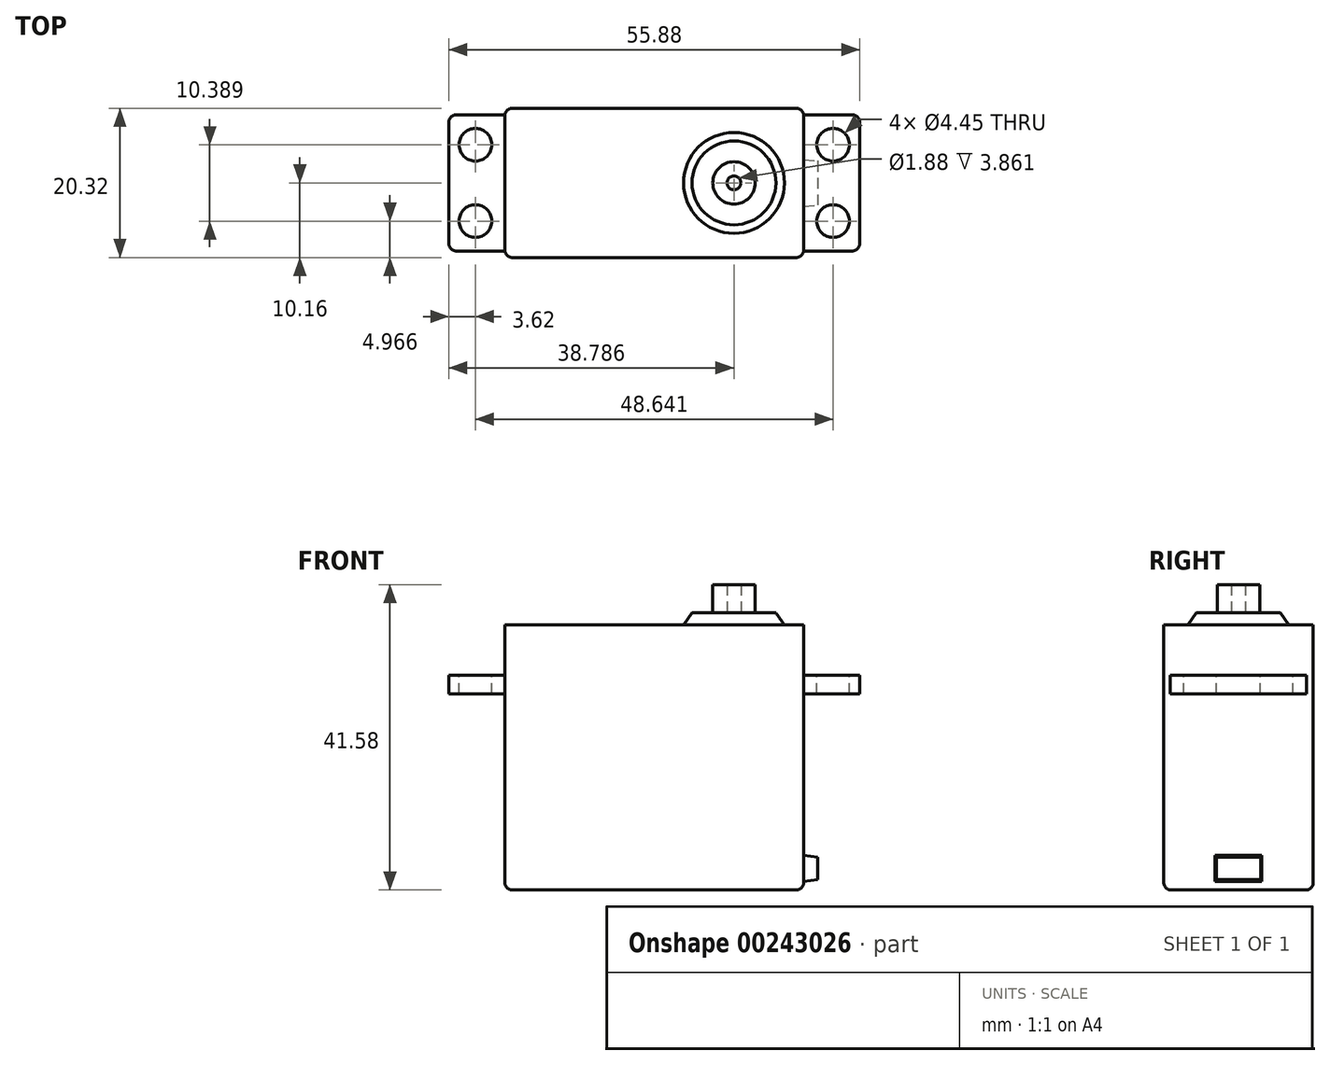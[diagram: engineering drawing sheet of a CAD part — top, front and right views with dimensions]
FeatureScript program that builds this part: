
annotation { "Feature Type Name" : "Feature", "Feature Type Description" : "" }
export const myFeature = defineFeature(function(context is Context, id is Id, definition is map)
    precondition{}
    {
        {
            var Q0;
            Q0=qCreatedBy(makeId("Top.planeOp"),FACE);
            var sketch = newSketch(context, id + "F0", { "sketchPlane" : qUnion([Q0])});
            skLineSegment(sketch, "E0.bottom", {"start": v(20.32, 10.16) * mm, "end": v(-20.32, 10.16) * mm});
            skLineSegment(sketch, "E0.top", {"start": v(20.32, -10.16) * mm, "end": v(-20.32, -10.16) * mm});
            skLineSegment(sketch, "E0.left", {"start": v(20.32, 10.16) * mm, "end": v(20.32, -10.16) * mm});
            skLineSegment(sketch, "E0.right", {"start": v(-20.32, 10.16) * mm, "end": v(-20.32, -10.16) * mm});
            skPoint(sketch, "E0.middle", {"position": v(0, 0) * mm});
            skSolve(sketch);
        }
        {
            var Q0;
            Q0 = qSketchRegion(id + "F0", true);
            extrude(context, id + "F1", {"entities" : qUnion([Q0]), "depth" : 36.07 * mm});
        }
        {
            var Q0;
            Q0=makeQuery(id+"F1.opExtrude","SWEPT_FACE",FACE,{"disambiguationData":[OSD([sQuery(id+"F0.wireOp",EDGE,"E0.left")])]});
            var sketch = newSketch(context, id + "F2", { "sketchPlane" : qUnion([Q0])});
            skLineSegment(sketch, "E1.bottom", {"start": v(3.18, 4.75) * mm, "end": v(-3.17, 4.75) * mm});
            skLineSegment(sketch, "E1.top", {"start": v(3.18, 1.14) * mm, "end": v(-3.17, 1.14) * mm});
            skLineSegment(sketch, "E1.left", {"start": v(3.18, 4.75) * mm, "end": v(3.18, 1.14) * mm});
            skLineSegment(sketch, "E1.right", {"start": v(-3.17, 4.75) * mm, "end": v(-3.17, 1.14) * mm});
            skPoint(sketch, "E1.middle", {"position": v(0, 2.95) * mm});
            skSolve(sketch);
        }
        {
            var Q0;
            Q0=makeQuery(id+"F2.imprint","IMPRINT",FACE,{"disambiguationData":[TD([[makeQuery(id+"F2.imprint","IMPRINT",EDGE,{"derivedFrom":sQuery(id+"F2.wireOp",EDGE,"E1.bottom")}),-1.0]])]});
            cPlane(context, id + "F3", {"entities" : qUnion([Q0]), "cplaneType" : CPlaneType.OFFSET, "offset" : 1.9 * mm, "width" : 152.4 * mm, "height" : 152.4 * mm});
        }
        {
            var Q0;
            Q0=qCreatedBy(id+"F3.planeOp",FACE);
            var sketch = newSketch(context, id + "F4", { "sketchPlane" : qUnion([Q0])});
            skPoint(sketch, "E2.0", {"position": v(0, 2.95) * mm});
            skLineSegment(sketch, "E3.bottom", {"start": v(3, 4.48) * mm, "end": v(-3, 4.48) * mm});
            skLineSegment(sketch, "E3.top", {"start": v(3, 1.4) * mm, "end": v(-3, 1.4) * mm});
            skLineSegment(sketch, "E3.left", {"start": v(3, 4.48) * mm, "end": v(3, 1.4) * mm});
            skLineSegment(sketch, "E3.right", {"start": v(-3, 4.48) * mm, "end": v(-3, 1.4) * mm});
            skSolve(sketch);
        }
        {
            var Q1;
            Q1=makeQuery(id+"F2.imprint","IMPRINT",FACE,{"disambiguationData":[TD([[makeQuery(id+"F2.imprint","IMPRINT",EDGE,{"derivedFrom":sQuery(id+"F2.wireOp",EDGE,"E1.bottom")}),1.0]])]});
            var Q2;
            Q2=makeQuery(id+"F4.imprint","IMPRINT",FACE,{"disambiguationData":[TD([[makeQuery(id+"F4.imprint","IMPRINT",EDGE,{"derivedFrom":sQuery(id+"F4.wireOp",EDGE,"E3.bottom")}),1.0]])]});
            loft(context, id + "F5", {"operationType" : NewBodyOperationType.ADD, "sheetProfilesArray" : [{ "sheetProfileEntities" : qUnion([Q1]) }, { "sheetProfileEntities" : qUnion([Q2]) }]});
        }
        {
            var Q0;
            Q0=makeQuery(id+"F1.opExtrude","CAP_FACE",FACE,{"disambiguationData":[OSD([sQuery(id+"F0.wireOp",EDGE,"E0.bottom"),sQuery(id+"F0.wireOp",EDGE,"E0.top"),sQuery(id+"F0.wireOp",EDGE,"E0.left"),sQuery(id+"F0.wireOp",EDGE,"E0.right")])],"isStart":false});
            cPlane(context, id + "F6", {"entities" : qUnion([Q0]), "cplaneType" : CPlaneType.OFFSET, "offset" : 6.86 * mm, "oppositeDirection" : true, "width" : 152.4 * mm, "height" : 152.4 * mm});
        }
        {
            var Q0;
            Q0=qCreatedBy(id+"F6.planeOp",FACE);
            var sketch = newSketch(context, id + "F7", { "sketchPlane" : qUnion([Q0])});
            skLineSegment(sketch, "E4.bottom", {"start": v(-26.92, -9.27) * mm, "end": v(-20.32, -9.27) * mm});
            skLineSegment(sketch, "E4.top", {"start": v(-26.92, 9.27) * mm, "end": v(-20.32, 9.27) * mm});
            skLineSegment(sketch, "E4.left", {"start": v(-27.94, -8.25) * mm, "end": v(-27.94, 8.26) * mm});
            skLineSegment(sketch, "E4.right", {"start": v(-20.32, -9.27) * mm, "end": v(-20.32, 9.27) * mm});
            skPoint(sketch, "E4.middle", {"position": v(-24.13, 0) * mm});
            skLineSegment(sketch, "E5.0", {"start": v(-20.32, 10.16) * mm, "end": v(-20.32, -10.16) * mm});
            skPoint(sketch, "E6.visualSharp", {"position": v(-27.94, -9.27) * mm});
            skArc(sketch, "E6.filletArc", {"start": v(-27.94, -8.25) * mm, "mid": v(-27.64, -8.97) * mm, "end": v(-26.92, -9.27) * mm});
            skPoint(sketch, "E7.visualSharp", {"position": v(-27.94, 9.27) * mm});
            skArc(sketch, "E7.filletArc", {"start": v(-26.92, 9.27) * mm, "mid": v(-27.64, 8.97) * mm, "end": v(-27.94, 8.26) * mm});
            skCircle(sketch, "E8", {"center": v(-24.32, -5.2) * mm, "radius": 2.22 * mm});
            skCircle(sketch, "E9.MirrorC", {"center": v(-24.32, 5.2) * mm, "radius": 2.22 * mm});
            skLineSegment(sketch, "E10.MirrorCS", {"start": v(26.92, 9.27) * mm, "end": v(20.32, 9.27) * mm});
            skArc(sketch, "E11.MirrorCS", {"start": v(26.92, 9.27) * mm, "mid": v(27.64, 8.97) * mm, "end": v(27.94, 8.26) * mm});
            skLineSegment(sketch, "E12.MirrorCS", {"start": v(27.94, -8.25) * mm, "end": v(27.94, 8.26) * mm});
            skArc(sketch, "E13.MirrorCS", {"start": v(27.94, -8.25) * mm, "mid": v(27.64, -8.97) * mm, "end": v(26.92, -9.27) * mm});
            skLineSegment(sketch, "E14.MirrorCS", {"start": v(26.92, -9.27) * mm, "end": v(20.32, -9.27) * mm});
            skCircle(sketch, "E15.MirrorC", {"center": v(24.32, -5.2) * mm, "radius": 2.22 * mm});
            skCircle(sketch, "E16.MirrorC", {"center": v(24.32, 5.2) * mm, "radius": 2.22 * mm});
            skLineSegment(sketch, "E17.MirrorCS", {"start": v(20.32, 10.16) * mm, "end": v(20.32, -10.16) * mm});
            skSolve(sketch);
        }
        {
            var Q0;
            Q0 = qSketchRegion(id + "F7", true);
            extrude(context, id + "F8", {"entities" : qUnion([Q0]), "operationType" : NewBodyOperationType.ADD, "oppositeDirection" : true, "depth" : 2.54 * mm});
        }
        {
            var Q0;
            Q0=makeQuery(id+"F1.opExtrude","CAP_FACE",FACE,{"disambiguationData":[OSD([sQuery(id+"F0.wireOp",EDGE,"E0.bottom"),sQuery(id+"F0.wireOp",EDGE,"E0.top"),sQuery(id+"F0.wireOp",EDGE,"E0.left"),sQuery(id+"F0.wireOp",EDGE,"E0.right")])],"isStart":false});
            var sketch = newSketch(context, id + "F9", { "sketchPlane" : qUnion([Q0])});
            skCircle(sketch, "E18", {"center": v(10.85, 0) * mm, "radius": 6.86 * mm});
            skSolve(sketch);
        }
        {
            var Q0;
            Q0=makeQuery(id+"F1.opExtrude","CAP_FACE",FACE,{"disambiguationData":[OSD([sQuery(id+"F0.wireOp",EDGE,"E0.bottom"),sQuery(id+"F0.wireOp",EDGE,"E0.top"),sQuery(id+"F0.wireOp",EDGE,"E0.left"),sQuery(id+"F0.wireOp",EDGE,"E0.right")])],"isStart":false});
            cPlane(context, id + "F10", {"entities" : qUnion([Q0]), "cplaneType" : CPlaneType.OFFSET, "offset" : 1.65 * mm, "width" : 152.4 * mm, "height" : 152.4 * mm});
        }
        {
            var Q0;
            Q0=qCreatedBy(id+"F10.planeOp",FACE);
            var sketch = newSketch(context, id + "F11", { "sketchPlane" : qUnion([Q0])});
            skPoint(sketch, "E19.0", {"position": v(10.85, 0) * mm});
            skCircle(sketch, "E20", {"center": v(10.85, 0) * mm, "radius": 5.7 * mm});
            skSolve(sketch);
        }
        {
            var Q1;
            Q1=makeQuery(id+"F9.imprint","IMPRINT",FACE,{"disambiguationData":[TD([[makeQuery(id+"F9.imprint","IMPRINT",EDGE,{"derivedFrom":sQuery(id+"F9.wireOp",EDGE,"E18")}),1.0]])]});
            var Q2;
            Q2=makeQuery(id+"F11.imprint","IMPRINT",FACE,{"disambiguationData":[TD([[makeQuery(id+"F11.imprint","IMPRINT",EDGE,{"derivedFrom":sQuery(id+"F11.wireOp",EDGE,"E20")}),1.0]])]});
            loft(context, id + "F12", {"operationType" : NewBodyOperationType.ADD, "sheetProfilesArray" : [{ "sheetProfileEntities" : qUnion([Q1]) }, { "sheetProfileEntities" : qUnion([Q2]) }]});
        }
        {
            var Q0;
            Q0=makeQuery(id+"F1.opExtrude","SWEPT_EDGE",EDGE,{"disambiguationData":[OSD([sQuery(id+"F0.wireOp",EDGE,"E0.top"),sQuery(id+"F0.wireOp",EDGE,"E0.left")])]});
            var Q1;
            Q1=makeQuery(id+"F1.opExtrude","SWEPT_EDGE",EDGE,{"disambiguationData":[OSD([sQuery(id+"F0.wireOp",EDGE,"E0.bottom"),sQuery(id+"F0.wireOp",EDGE,"E0.left")])]});
            var Q2;
            Q2=makeQuery(id+"F1.opExtrude","SWEPT_EDGE",EDGE,{"disambiguationData":[OSD([sQuery(id+"F0.wireOp",EDGE,"E0.bottom"),sQuery(id+"F0.wireOp",EDGE,"E0.right")])]});
            var Q3;
            Q3=makeQuery(id+"F1.opExtrude","SWEPT_EDGE",EDGE,{"disambiguationData":[OSD([sQuery(id+"F0.wireOp",EDGE,"E0.top"),sQuery(id+"F0.wireOp",EDGE,"E0.right")])]});
            var Q4;
            Q4=makeQuery(id+"F1.opExtrude","CAP_EDGE",EDGE,{"disambiguationData":[OSD([sQuery(id+"F0.wireOp",EDGE,"E0.top")])],"isStart":true});
            var Q5;
            Q5=makeQuery(id+"F1.opExtrude","CAP_EDGE",EDGE,{"disambiguationData":[OSD([sQuery(id+"F0.wireOp",EDGE,"E0.left")])],"isStart":true});
            var Q6;
            Q6=makeQuery(id+"F1.opExtrude","CAP_EDGE",EDGE,{"disambiguationData":[OSD([sQuery(id+"F0.wireOp",EDGE,"E0.bottom")])],"isStart":true});
            var Q7;
            Q7=makeQuery(id+"F1.opExtrude","CAP_EDGE",EDGE,{"disambiguationData":[OSD([sQuery(id+"F0.wireOp",EDGE,"E0.right")])],"isStart":true});
            fillet(context, id + "F13", {"entities" : qUnion([Q0, Q1, Q2, Q3, Q4, Q5, Q6, Q7]), "radius" : 1.02 * mm, "tangentPropagation" : true, "allowEdgeOverflow" : false});
        }
        {
            var Q0;
            Q0=makeQuery(id+"F12.opLoft","CAP_FACE",FACE,{"disambiguationData":[OSD([makeQuery(id+"F11.imprint","IMPRINT",FACE,{"disambiguationData":[TD([[makeQuery(id+"F11.imprint","IMPRINT",EDGE,{"derivedFrom":sQuery(id+"F11.wireOp",EDGE,"E20")}),1.0]])]})])],"isStart":true});
            var sketch = newSketch(context, id + "F14", { "sketchPlane" : qUnion([Q0])});
            skPoint(sketch, "E21.0", {"position": v(10.85, 0) * mm});
            skCircle(sketch, "E22", {"center": v(10.85, 0) * mm, "radius": 2.88 * mm});
            skCircle(sketch, "E23", {"center": v(10.85, 0) * mm, "radius": 0.94 * mm});
            skSolve(sketch);
        }
        {
            var Q0;
            Q0 = qSketchRegion(id + "F14", true);
            extrude(context, id + "F15", {"entities" : qUnion([Q0]), "operationType" : NewBodyOperationType.ADD, "depth" : 3.86 * mm});
        }
    });
